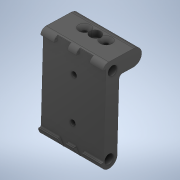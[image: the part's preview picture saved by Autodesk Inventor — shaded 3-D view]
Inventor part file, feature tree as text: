
AUTODESK INVENTOR PART (.ipt)
format: ipt  version: 2020 (Build 240168000, 168)  size: 340,992 bytes
history: native  units: in
note: dims shown in document units (in); Inventor stores cm internally (conversion verified against a paired STEP export)
features: extrude x6, sketch x6, projected_geometry x2
ambient origin geometry x8: Origin, YZ Plane, XZ Plane, XY Plane, X Axis, Y Axis, Z Axis, Center Point
bodies: Solid2 (feature_tree), Solid1 (feature_tree)
feature tree (14):
  extrude  "Extrusion1"  Depth=0.126in
  extrude  "add 5mm left"  Depth=0.1969in TaperAngle=0.0deg
  extrude  "add 5mm right"  Depth=0.1181in
  extrude  "fin mount holes"  Depth=0.3937in TaperAngle=0.0deg
  extrude  "add standoff holes"  Depth=0.2008in
  extrude  "add nuts for mounting"  Depth=0.2205in
  sketch  "Sketch1"  dims[d0=0.126in d1=0.126in]
  sketch  "Sketch2"  dims[d2=0.3937in d3=0.0in d4=0.1969in d5=0.0in]
  projected_geometry  "Projected Loop1"
  sketch  "Sketch3"  dims[d6=0.1969in d7=0.0in d8=0.1181in]
  projected_geometry  "Projected Loop2"
  sketch  "Sketch4"  dims[d9=0.1181in d10=0.3937in d11=0.0in]
  sketch  "Sketch5"  dims[d12=0.2008in d13=0.2008in]
  sketch  "Sketch6"  dims[d14=0.3937in d15=0.0in d16=0.2205in d17=0.2205in d18=0.0984in d19=0.0in]
